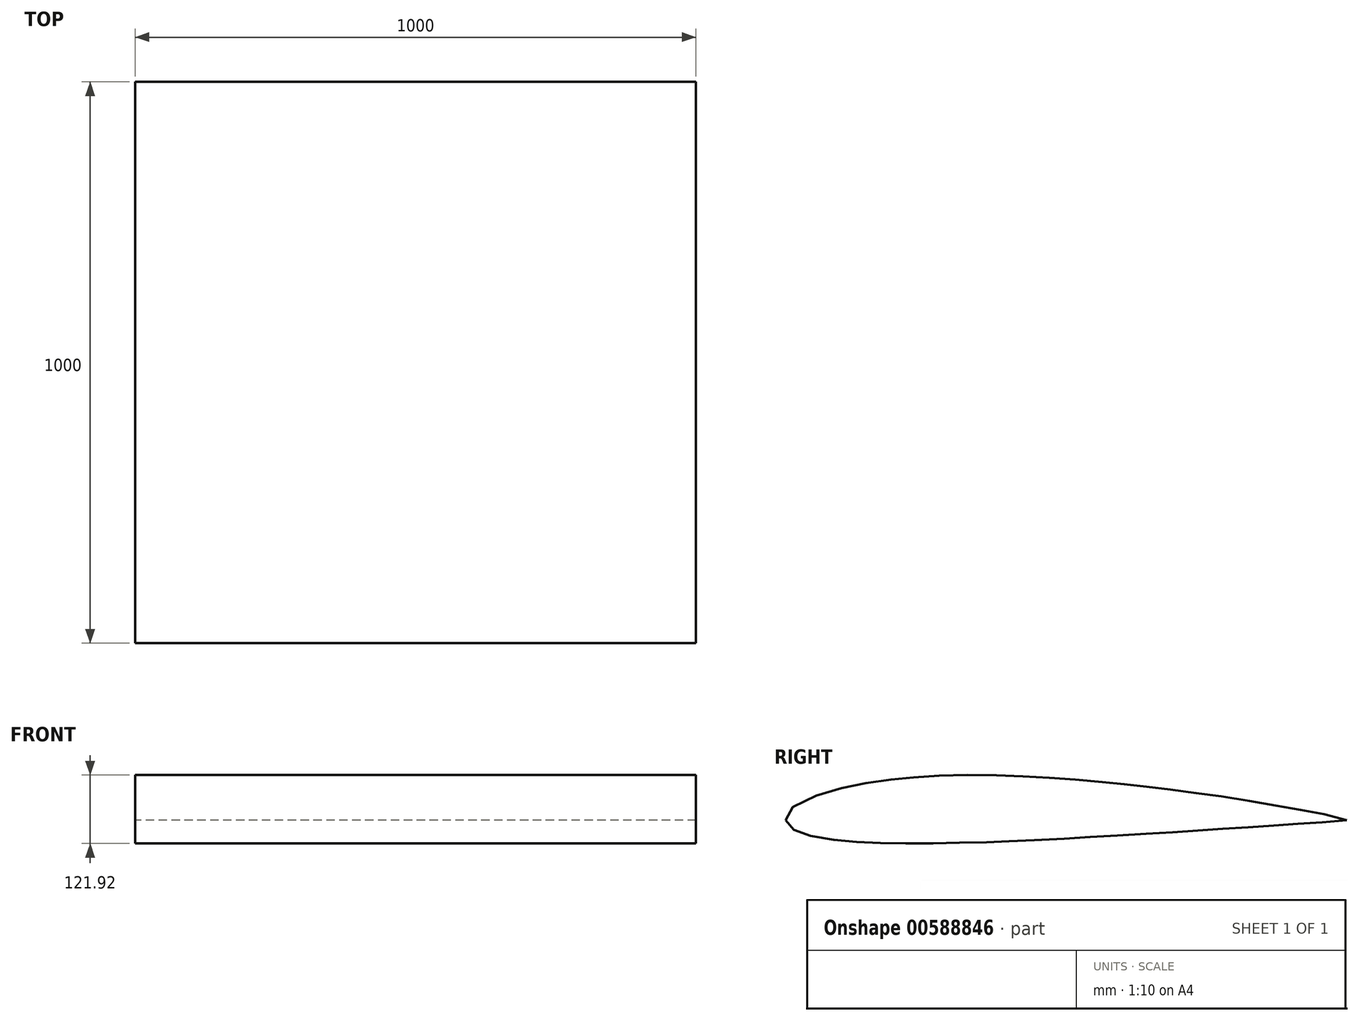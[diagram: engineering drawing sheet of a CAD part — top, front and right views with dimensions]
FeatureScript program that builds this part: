
annotation { "Feature Type Name" : "Feature", "Feature Type Description" : "" }
export const myFeature = defineFeature(function(context is Context, id is Id, definition is map)
    precondition{}
    {
        {
            var Q0;
            Q0=qCreatedBy(makeId("Right.planeOp"),FACE);
            var sketch = newSketch(context, id + "F0", { "sketchPlane" : qUnion([Q0])});
            skLineSegment(sketch, "E0", {"start": v(0, 0) * mm, "end": v(1000, 0) * mm, "construction": true});
            skFitSpline(sketch, "E1", {"points": [v(0, 0) * mm, v(3.2, 13.06) * mm, v(15.34, 25.24) * mm, v(58.15, 45.18) * mm, v(99.86, 57.07) * mm, v(138.64, 65.12) * mm, v(181.08, 71.52) * mm, v(211.27, 74.81) * mm, v(252.43, 77.74) * mm, v(295.23, 79.75) * mm, v(352.3, 80.12) * mm, v(399.5, 79.02) * mm, v(443.6, 76.64) * mm, v(488.05, 74.26) * mm, v(532.68, 70.79) * mm, v(577.14, 66.76) * mm, v(604.4, 64.02) * mm, v(636.6, 60.18) * mm, v(672.63, 55.79) * mm, v(713.6, 50.67) * mm, v(755.68, 45) * mm, v(799.22, 38.6) * mm, v(852.64, 29.81) * mm, v(889.77, 23.04) * mm, v(931.48, 15.73) * mm, v(966.42, 8.96) * mm, v(1000, 0) * mm], "startDerivative": vector(0, 733.33) * mm, "endDerivative": vector(433.82, -233.49) * mm});
            skFitSpline(sketch, "E2", {"points": [v(0, 0) * mm, v(1.08, -5.36) * mm, v(9.81, -14.55) * mm, v(29.01, -23.88) * mm, v(47.62, -29.2) * mm, v(83.57, -35.12) * mm, v(117.4, -38.32) * mm, v(152.86, -40.45) * mm, v(190.56, -41.42) * mm, v(234.46, -41.7) * mm, v(281.94, -41.03) * mm, v(325.06, -40.06) * mm, v(370.83, -38.83) * mm, v(400.37, -37.46) * mm, v(440.34, -35.82) * mm, v(497.51, -33.07) * mm, v(540.41, -30.51) * mm, v(586.88, -27.77) * mm, v(638.83, -24.75) * mm, v(683.65, -22) * mm, v(725, -19.44) * mm, v(765.51, -16.6) * mm, v(804.66, -13.86) * mm, v(846.28, -11.3) * mm, v(886.61, -8.56) * mm, v(924.04, -5.83) * mm, v(961.6, -3.59) * mm, v(1000, 0) * mm], "startDerivative": vector(0, -299.02) * mm, "endDerivative": vector(970.9, 129.72) * mm});
            skSolve(sketch);
        }
        {
            var Q0;
            Q0=qSketchRegion(id+"F0",true);
            extrude(context, id + "F1", {"entities" : qUnion([Q0]), "depth" : 1000 * mm});
        }
    });
